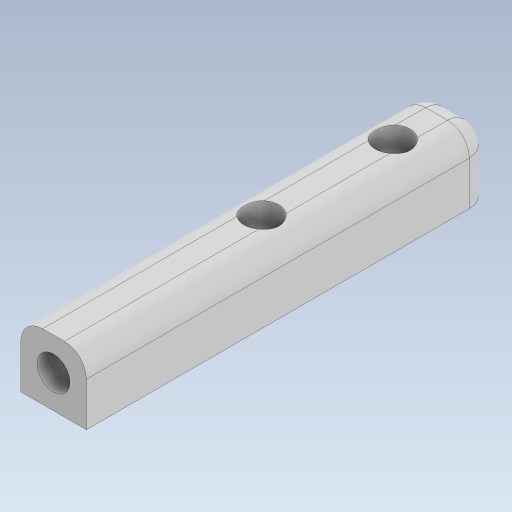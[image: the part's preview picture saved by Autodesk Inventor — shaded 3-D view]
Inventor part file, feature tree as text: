
AUTODESK INVENTOR PART (.ipt)
format: ipt  version: 2023.5 (Build 275446000, 446)  size: 136,192 bytes
history: native  units: mm
features: extrude x2, sketch x2, fillet x1
ambient origin geometry x8: Origin, YZ Plane, XZ Plane, XY Plane, X Axis, Y Axis, Z Axis, Center Point
bodies: Solid1 (feature_tree)
feature tree (5):
  extrude  "Extrusion1"  Depth=3.2mm
  extrude  "Extrusion2"  Depth=2.0mm
  fillet  "Fillet1"  Radius=6.0mm
  sketch  "Sketch1"  dims[d0=3.2mm d1=3.2mm]
  sketch  "Sketch2"  dims[d2=12.0mm d3=19.0mm d5=6.0mm d6=0.0mm d7=3.0mm d8=3.0mm d9=3.0mm d10=10.0mm d11=0.0mm d12=2.0mm]
